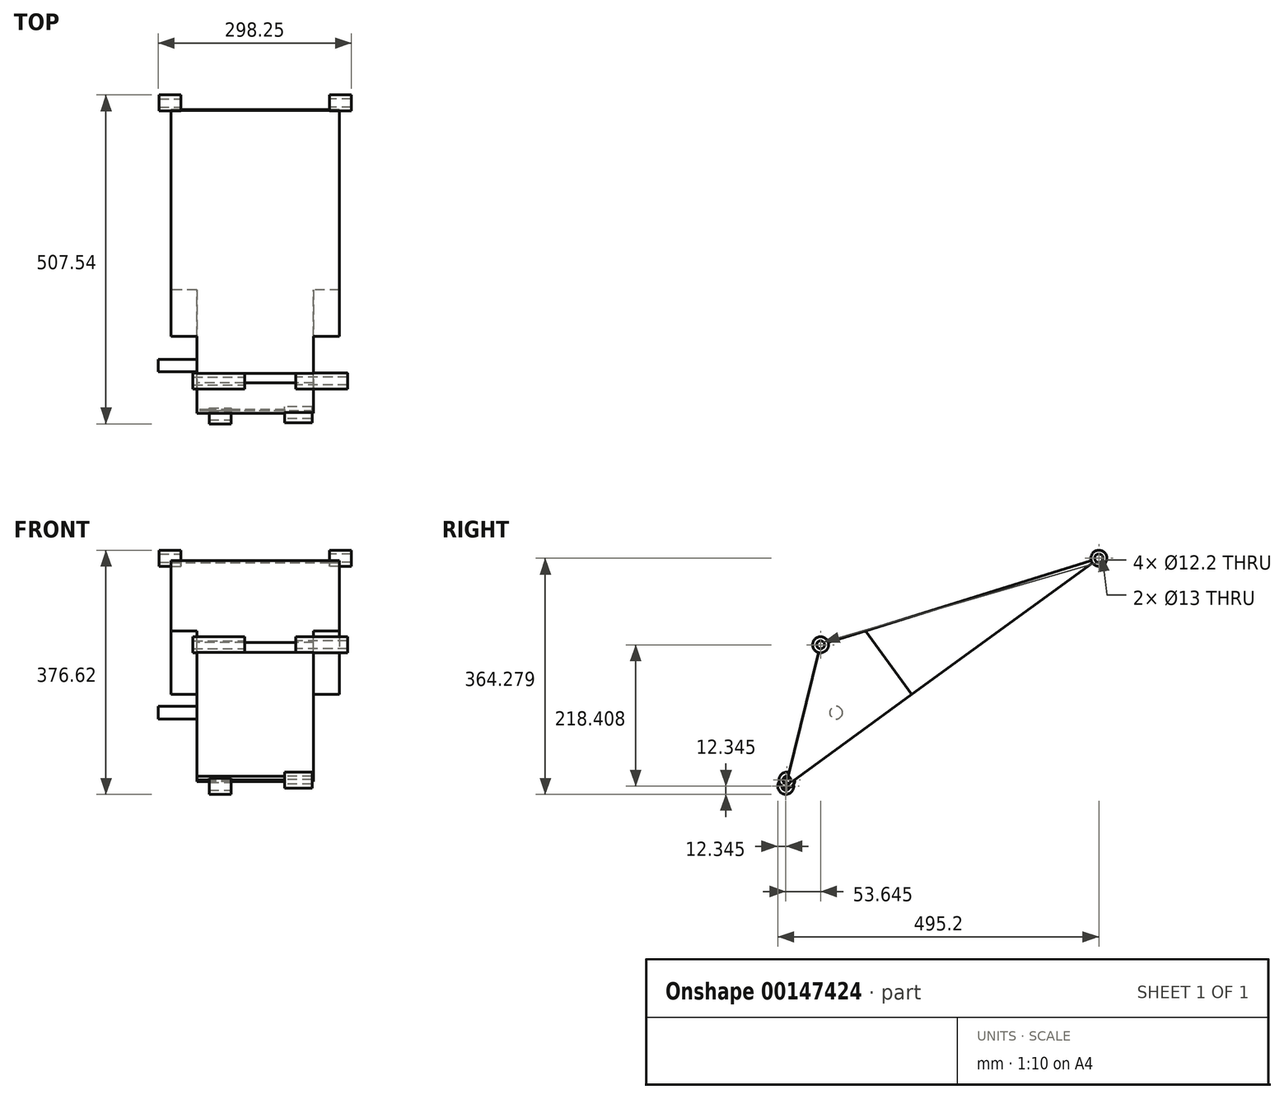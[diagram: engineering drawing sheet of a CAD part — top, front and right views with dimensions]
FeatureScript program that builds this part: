
annotation { "Feature Type Name" : "Feature", "Feature Type Description" : "" }
export const myFeature = defineFeature(function(context is Context, id is Id, definition is map)
    precondition{}
    {
        {
            var Q0;
            Q0=qCreatedBy(makeId("Right.planeOp"),FACE);
            var sketch = newSketch(context, id + "F0", { "sketchPlane" : qUnion([Q0])});
            skCircle(sketch, "E0", {"center": v(-23.94, 18.58) * mm, "radius": 12.34 * mm});
            skCircle(sketch, "E1", {"center": v(-23.94, 18.58) * mm, "radius": 6.1 * mm});
            skCircle(sketch, "E2", {"center": v(-77.58, -199.82) * mm, "radius": 6.1 * mm});
            skCircle(sketch, "E3", {"center": v(-77.58, -199.82) * mm, "radius": 12.34 * mm});
            skCircle(sketch, "E4", {"center": v(405.27, 152.1) * mm, "radius": 6.5 * mm});
            skCircle(sketch, "E5", {"center": v(405.27, 152.1) * mm, "radius": 12.34 * mm});
            skLineSegment(sketch, "E6", {"start": v(-23.94, 18.58) * mm, "end": v(405.27, 152.1) * mm});
            skLineSegment(sketch, "E7", {"start": v(405.27, 152.1) * mm, "end": v(-77.58, -199.82) * mm});
            skLineSegment(sketch, "E8", {"start": v(-77.58, -199.82) * mm, "end": v(-23.94, 18.58) * mm});
            skCircle(sketch, "E9", {"center": v(0.04, -86.2) * mm, "radius": 9.8 * mm});
            skCircle(sketch, "E10", {"center": v(-75.84, -190.26) * mm, "radius": 6.1 * mm});
            skCircle(sketch, "E11", {"center": v(-75.84, -190.26) * mm, "radius": 12.34 * mm});
            skLineSegment(sketch, "E12", {"start": v(45.24, 40.1) * mm, "end": v(116.83, -58.12) * mm});
            skSolve(sketch);
        }
        {
            var Q0;
            Q0=makeQuery(id+"F0.imprint","IMPRINT",FACE,{"disambiguationData":[TD([[makeQuery(id+"F0.imprint","IMPRINT",EDGE,{"derivedFrom":sQuery(id+"F0.wireOp",EDGE,"E0")}),1.0]])]});
            extrude(context, id + "F1", {"entities" : qUnion([Q0]), "oppositeDirection" : true, "depth" : (296.5 / 2 - 52) * mm, "hasSecondDirection" : true, "secondDirectionOppositeDirection" : true, "secondDirectionDepth" : (296.5 / 2 - 52 - 79.6) * mm});
        }
        {
            var Q0;
            Q0=makeQuery(id+"F0.imprint","IMPRINT",FACE,{"disambiguationData":[TD([[makeQuery(id+"F0.imprint","IMPRINT",EDGE,{"derivedFrom":sQuery(id+"F0.wireOp",EDGE,"E2")}),-1.0]])]});
            extrude(context, id + "F2", {"entities" : qUnion([Q0]), "oppositeDirection" : true, "depth" : (296.5 / 2 - 52 - 25) * mm, "hasSecondDirection" : true, "secondDirectionOppositeDirection" : true, "secondDirectionDepth" : (71.25 - 34) * mm});
        }
        {
            var Q0;
            Q0=makeQuery(id+"F0.imprint","IMPRINT",FACE,{"disambiguationData":[TD([[makeQuery(id+"F0.imprint","IMPRINT",EDGE,{"derivedFrom":sQuery(id+"F0.wireOp",EDGE,"E4")}),-1.0]])]});
            extrude(context, id + "F3", {"entities" : qUnion([Q0]), "oppositeDirection" : true, "depth" : (296.5 / 2) * mm, "hasSecondDirection" : true, "secondDirectionOppositeDirection" : true, "secondDirectionDepth" : (296.5 / 2 - 33.5) * mm});
        }
        {
            var Q0;
            {var subQ0=sQuery(id+"F0.wireOp",EDGE,"E6");var subQ1=sQuery(id+"F0.wireOp",EDGE,"E0");var subQ2=makeQuery(id+"F0.imprint","INTERSECT",VERTEX,{"derivedFrom":[subQ1,subQ0]});Q0=makeQuery(id+"F0.imprint","IMPRINT",FACE,{"disambiguationData":[TD([[makeQuery(id+"F0.imprint","IMPRINT",EDGE,{"disambiguationData":[TD([[subQ2,-1.0]])],"derivedFrom":subQ1}),1.0]])]});}
            var Q1;
            {var subQ0=sQuery(id+"F0.wireOp",EDGE,"E6");var subQ1=sQuery(id+"F0.wireOp",EDGE,"E0");var subQ2=makeQuery(id+"F0.imprint","INTERSECT",VERTEX,{"derivedFrom":[subQ1,subQ0]});Q1=makeQuery(id+"F0.imprint","IMPRINT",FACE,{"disambiguationData":[TD([[makeQuery(id+"F0.imprint","IMPRINT",EDGE,{"disambiguationData":[TD([[subQ2,1.0]])],"derivedFrom":subQ1}),1.0]])]});}
            extrude(context, id + "F4", {"entities" : qUnion([Q0, Q1]), "depth" : (-296.5 / 2 + 52 + 238.6) * mm, "hasSecondDirection" : true, "secondDirectionOppositeDirection" : false, "secondDirectionDepth" : (142.35 - 79.6) * mm});
        }
        {
            var Q0;
            {var subQ0=sQuery(id+"F0.wireOp",EDGE,"E7");var subQ1=sQuery(id+"F0.wireOp",EDGE,"E2");var subQ2=makeQuery(id+"F0.imprint","INTERSECT",VERTEX,{"derivedFrom":[subQ1,subQ0]});Q0=makeQuery(id+"F0.imprint","IMPRINT",FACE,{"disambiguationData":[TD([[makeQuery(id+"F0.imprint","IMPRINT",EDGE,{"disambiguationData":[TD([[subQ2,1.0]])],"derivedFrom":subQ1}),-1.0]])]});}
            var Q1;
            {var subQ0=sQuery(id+"F0.wireOp",EDGE,"E7");var subQ1=sQuery(id+"F0.wireOp",EDGE,"E2");var subQ2=makeQuery(id+"F0.imprint","INTERSECT",VERTEX,{"derivedFrom":[subQ1,subQ0]});Q1=makeQuery(id+"F0.imprint","IMPRINT",FACE,{"disambiguationData":[TD([[makeQuery(id+"F0.imprint","IMPRINT",EDGE,{"disambiguationData":[TD([[subQ2,-1.0]])],"derivedFrom":subQ1}),-1.0]])]});}
            var Q2;
            {var subQ0=sQuery(id+"F0.wireOp",EDGE,"E11");var subQ1=sQuery(id+"F0.wireOp",EDGE,"E3");var subQ2=makeQuery(id+"F0.imprint","INTERSECT",VERTEX,{"disambiguationData":[OD(0.0)],"derivedFrom":[subQ1,subQ0]});Q2=makeQuery(id+"F0.imprint","IMPRINT",FACE,{"disambiguationData":[TD([[makeQuery(id+"F0.imprint","IMPRINT",EDGE,{"disambiguationData":[TD([[subQ2,-1.0]])],"derivedFrom":subQ1}),-1.0]])]});}
            var Q3;
            {var subQ5=sQuery(id+"F0.wireOp",EDGE,"E3");var subQ7=sQuery(id+"F0.wireOp",EDGE,"E7");var subQ9=makeQuery(id+"F0.imprint","INTERSECT",VERTEX,{"derivedFrom":[subQ5,subQ7]});Q3=makeQuery(id+"F0.imprint","IMPRINT",FACE,{"disambiguationData":[TD([[makeQuery(id+"F0.imprint","IMPRINT",EDGE,{"disambiguationData":[TD([[subQ9,-1.0]])],"derivedFrom":subQ5}),-1.0]])]});}
            var Q4;
            {var subQ0=sQuery(id+"F0.wireOp",EDGE,"E11");var subQ1=sQuery(id+"F0.wireOp",EDGE,"E3");var subQ2=makeQuery(id+"F0.imprint","INTERSECT",VERTEX,{"disambiguationData":[OD(1.0)],"derivedFrom":[subQ1,subQ0]});Q4=makeQuery(id+"F0.imprint","IMPRINT",FACE,{"disambiguationData":[TD([[makeQuery(id+"F0.imprint","IMPRINT",EDGE,{"disambiguationData":[TD([[subQ2,1.0]])],"derivedFrom":subQ1}),-1.0]])]});}
            var Q5;
            {var subQ0=sQuery(id+"F0.wireOp",EDGE,"E10");var subQ1=sQuery(id+"F0.wireOp",EDGE,"E2");var subQ2=makeQuery(id+"F0.imprint","INTERSECT",VERTEX,{"disambiguationData":[OD(1.0)],"derivedFrom":[subQ1,subQ0]});Q5=makeQuery(id+"F0.imprint","IMPRINT",FACE,{"disambiguationData":[TD([[makeQuery(id+"F0.imprint","IMPRINT",EDGE,{"disambiguationData":[TD([[subQ2,-1.0]])],"derivedFrom":subQ1}),-1.0]])]});}
            var Q6;
            {var subQ3=sQuery(id+"F0.wireOp",EDGE,"E10");var subQ5=sQuery(id+"F0.wireOp",EDGE,"E2");var subQ9=makeQuery(id+"F0.imprint","INTERSECT",VERTEX,{"disambiguationData":[OD(1.0)],"derivedFrom":[subQ5,subQ3]});Q6=makeQuery(id+"F0.imprint","IMPRINT",FACE,{"disambiguationData":[TD([[makeQuery(id+"F0.imprint","IMPRINT",EDGE,{"disambiguationData":[TD([[subQ9,-1.0]])],"derivedFrom":subQ5}),1.0]])]});}
            var Q7;
            {var subQ0=sQuery(id+"F0.wireOp",EDGE,"E10");var subQ1=sQuery(id+"F0.wireOp",EDGE,"E2");var subQ2=makeQuery(id+"F0.imprint","INTERSECT",VERTEX,{"disambiguationData":[OD(0.0)],"derivedFrom":[subQ1,subQ0]});Q7=makeQuery(id+"F0.imprint","IMPRINT",FACE,{"disambiguationData":[TD([[makeQuery(id+"F0.imprint","IMPRINT",EDGE,{"disambiguationData":[TD([[subQ2,1.0]])],"derivedFrom":subQ1}),1.0]])]});}
            extrude(context, id + "F5", {"entities" : qUnion([Q0, Q1, Q2, Q3, Q4, Q5, Q6, Q7]), "depth" : (-296.5 / 2 + 52 + 25 + 158.8) * mm, "hasSecondDirection" : true, "secondDirectionOppositeDirection" : false, "secondDirectionDepth" : (87.55 - 42) * mm});
        }
        {
            var Q0;
            Q0=makeQuery(id+"F0.imprint","IMPRINT",FACE,{"disambiguationData":[TD([[makeQuery(id+"F0.imprint","IMPRINT",EDGE,{"derivedFrom":sQuery(id+"F0.wireOp",EDGE,"E9")}),1.0]])]});
            extrude(context, id + "F6", {"entities" : qUnion([Q0]), "oppositeDirection" : true, "depth" : 150 * mm});
        }
        {
            var Q0;
            Q0=makeQuery(id+"F3.opExtrude","SWEPT_BODY",BODY,{"disambiguationData":[OSD([sQuery(id+"F0.wireOp",EDGE,"E4"),sQuery(id+"F0.wireOp",EDGE,"E5")])]});
            var Q1;
            Q1=qCreatedBy(makeId("Right.planeOp"),FACE);
            mirror(context, id + "F7", {"entities" : qUnion([Q0]), "mirrorPlane" : qUnion([Q1])});
        }
        {
            var Q0;
            {var subQ0=sQuery(id+"F0.wireOp",EDGE,"E6");var subQ1=sQuery(id+"F0.wireOp",EDGE,"E0");var subQ2=makeQuery(id+"F0.imprint","INTERSECT",VERTEX,{"derivedFrom":[subQ1,subQ0]});Q0=makeQuery(id+"F0.imprint","IMPRINT",FACE,{"disambiguationData":[TD([[makeQuery(id+"F0.imprint","IMPRINT",EDGE,{"disambiguationData":[TD([[subQ2,1.0]])],"derivedFrom":subQ1}),-1.0]])]});}
            var Q1;
            Q1=makeQuery(id+"F0.imprint","IMPRINT",FACE,{"disambiguationData":[TD([[makeQuery(id+"F0.imprint","IMPRINT",EDGE,{"derivedFrom":sQuery(id+"F0.wireOp",EDGE,"E9")}),1.0]])]});
            var Q2;
            {var subQ5=sQuery(id+"F0.wireOp",EDGE,"E3");var subQ7=sQuery(id+"F0.wireOp",EDGE,"E7");var subQ9=makeQuery(id+"F0.imprint","INTERSECT",VERTEX,{"derivedFrom":[subQ5,subQ7]});Q2=makeQuery(id+"F0.imprint","IMPRINT",FACE,{"disambiguationData":[TD([[makeQuery(id+"F0.imprint","IMPRINT",EDGE,{"disambiguationData":[TD([[subQ9,-1.0]])],"derivedFrom":subQ5}),-1.0]])]});}
            extrude(context, id + "F8", {"entities" : qUnion([Q0, Q1, Q2]), "operationType" : NewBodyOperationType.ADD, "endBound" : BoundingType.SYMMETRIC, "depth" : 180 * mm});
        }
        {
            var Q0;
            {var subQ5=sQuery(id+"F0.wireOp",EDGE,"E12");Q0=makeQuery(id+"F0.imprint","IMPRINT",FACE,{"disambiguationData":[TD([[makeQuery(id+"F0.imprint","IMPRINT",EDGE,{"derivedFrom":subQ5}),1.0]])]});}
            extrude(context, id + "F9", {"entities" : qUnion([Q0]), "operationType" : NewBodyOperationType.ADD, "endBound" : BoundingType.SYMMETRIC, "depth" : 260 * mm});
        }
    });
